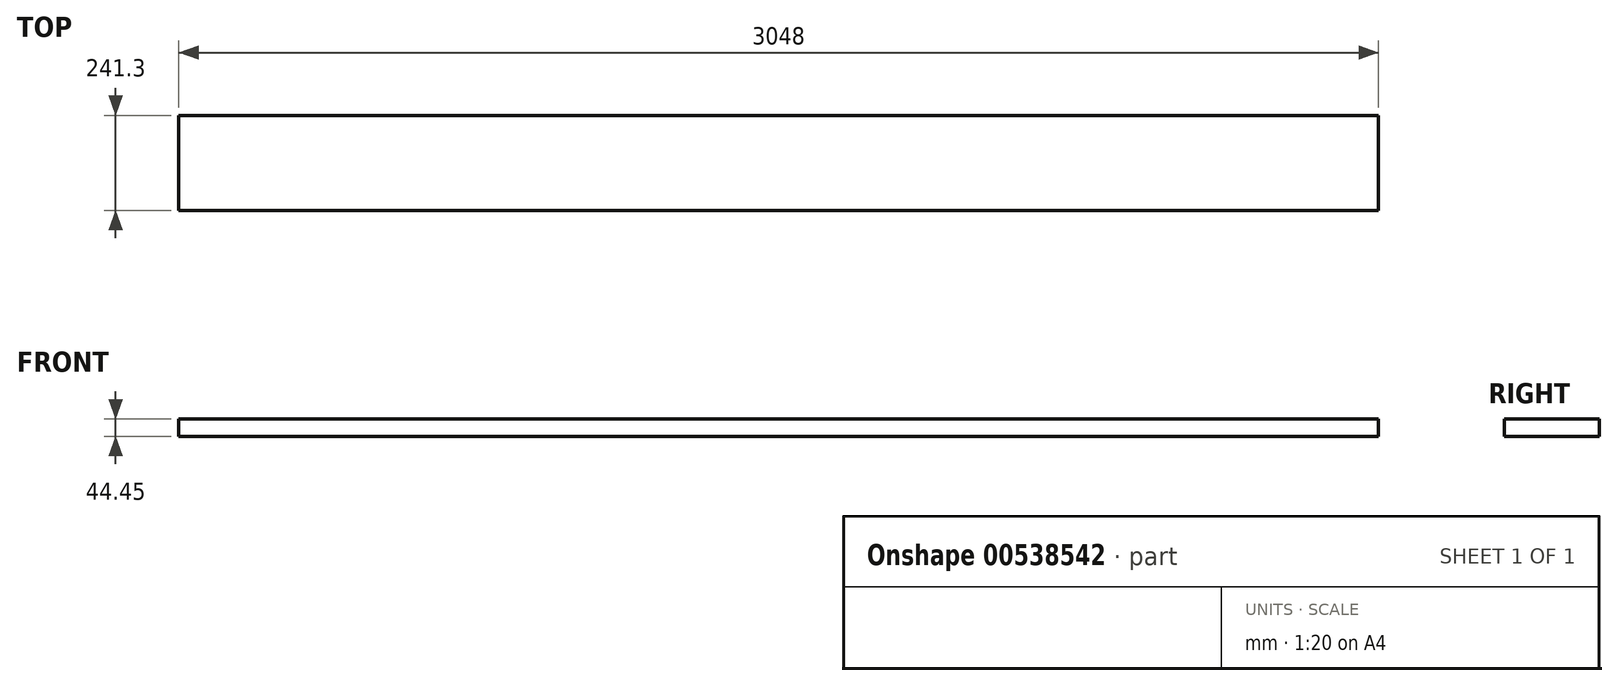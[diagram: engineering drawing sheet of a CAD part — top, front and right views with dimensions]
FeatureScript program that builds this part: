
annotation { "Feature Type Name" : "Feature", "Feature Type Description" : "" }
export const myFeature = defineFeature(function(context is Context, id is Id, definition is map)
    precondition{}
    {
        {
            var Q0;
            Q0=qCreatedBy(makeId("Top.planeOp"),FACE);
            var sketch = newSketch(context, id + "F0", { "sketchPlane" : qUnion([Q0])});
            skLineSegment(sketch, "E0.bottom", {"start": v(-1524, 120.65) * mm, "end": v(1524, 120.65) * mm});
            skLineSegment(sketch, "E0.top", {"start": v(-1524, -120.65) * mm, "end": v(1524, -120.65) * mm});
            skLineSegment(sketch, "E0.left", {"start": v(-1524, 120.65) * mm, "end": v(-1524, -120.65) * mm});
            skLineSegment(sketch, "E0.right", {"start": v(1524, 120.65) * mm, "end": v(1524, -120.65) * mm});
            skPoint(sketch, "E0.middle", {"position": v(0, 0) * mm});
            skSolve(sketch);
        }
        {
            var Q0;
            Q0=makeQuery(id+"F0.imprint","IMPRINT",FACE,{"disambiguationData":[TD([[makeQuery(id+"F0.imprint","IMPRINT",EDGE,{"derivedFrom":sQuery(id+"F0.wireOp",EDGE,"E0.bottom")}),-1.0]])]});
            extrude(context, id + "F1", {"entities" : qUnion([Q0]), "depth" : 44.45 * mm, "offsetDistance" : 25.4 * mm});
        }
    });
